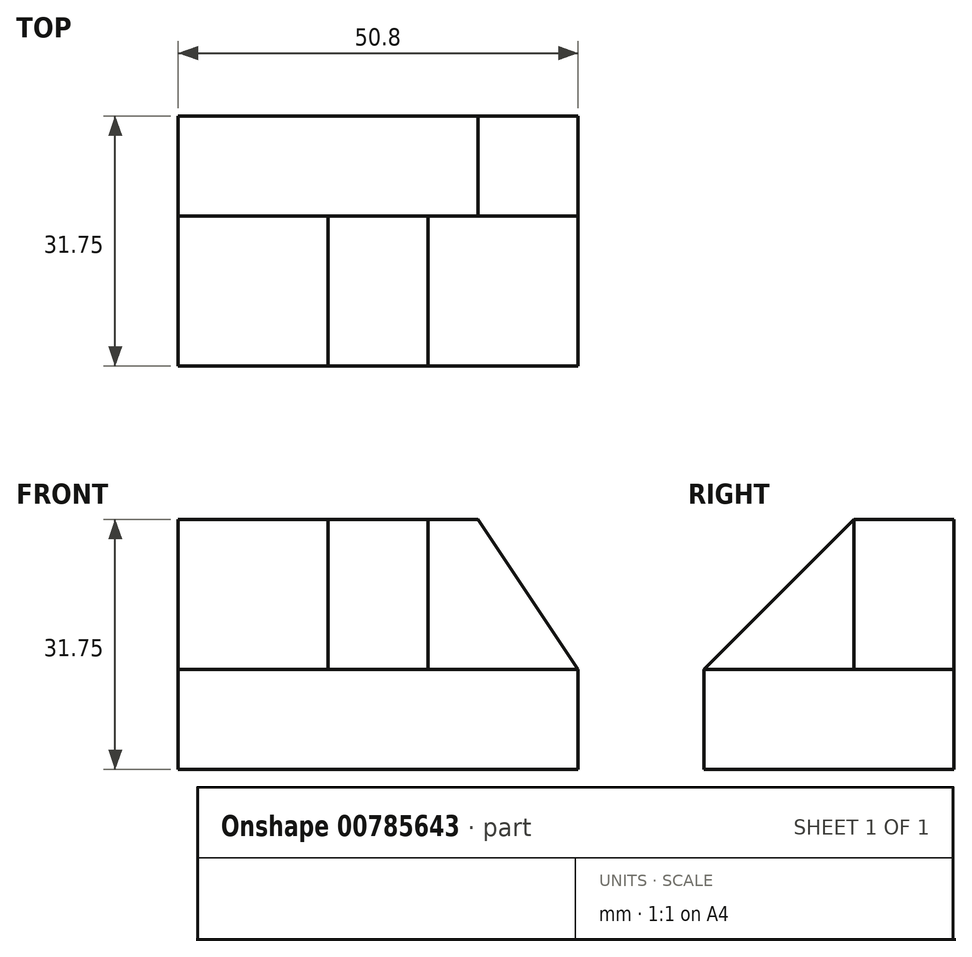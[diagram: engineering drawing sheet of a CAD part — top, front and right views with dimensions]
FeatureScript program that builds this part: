
annotation { "Feature Type Name" : "Feature", "Feature Type Description" : "" }
export const myFeature = defineFeature(function(context is Context, id is Id, definition is map)
    precondition{}
    {
        {
            var Q0;
            Q0=qCreatedBy(makeId("Front.planeOp"),FACE);
            var sketch = newSketch(context, id + "F0", { "sketchPlane" : qUnion([Q0])});
            skLineSegment(sketch, "E0", {"start": v(0, 0) * mm, "end": v(-50.8, 0) * mm});
            skLineSegment(sketch, "E1", {"start": v(-50.8, 0) * mm, "end": v(-50.8, 31.75) * mm});
            skLineSegment(sketch, "E2", {"start": v(-50.8, 31.75) * mm, "end": v(0, 31.75) * mm});
            skLineSegment(sketch, "E3", {"start": v(0, 31.75) * mm, "end": v(0, 0) * mm});
            skSolve(sketch);
        }
        {
            var Q0;
            Q0=makeQuery(id+"F0.imprint","IMPRINT",FACE,{"disambiguationData":[TD([[makeQuery(id+"F0.imprint","IMPRINT",EDGE,{"derivedFrom":sQuery(id+"F0.wireOp",EDGE,"E0")}),-1.0]])]});
            extrude(context, id + "F1", {"entities" : qUnion([Q0]), "depth" : 31.75 * mm, "offsetDistance" : 25.4 * mm});
        }
        {
            var Q0;
            Q0=makeQuery(id+"F1.opExtrude","CAP_FACE",FACE,{"disambiguationData":[OSD([sQuery(id+"F0.wireOp",EDGE,"E0"),sQuery(id+"F0.wireOp",EDGE,"E1"),sQuery(id+"F0.wireOp",EDGE,"E2"),sQuery(id+"F0.wireOp",EDGE,"E3")])],"isStart":false});
            var sketch = newSketch(context, id + "F2", { "sketchPlane" : qUnion([Q0])});
            skLineSegment(sketch, "E4", {"start": v(-50.8, 0) * mm, "end": v(-50.8, 12.7) * mm});
            skLineSegment(sketch, "E5", {"start": v(-50.8, 12.7) * mm, "end": v(0, 12.7) * mm});
            skLineSegment(sketch, "E6", {"start": v(0, 12.7) * mm, "end": v(0, 0) * mm});
            skLineSegment(sketch, "E7", {"start": v(0, 0) * mm, "end": v(-50.8, 0) * mm});
            skLineSegment(sketch, "E8", {"start": v(0, 12.7) * mm, "end": v(0, 31.75) * mm});
            skLineSegment(sketch, "E9", {"start": v(0, 31.75) * mm, "end": v(-19.05, 31.75) * mm});
            skLineSegment(sketch, "E10", {"start": v(-19.05, 31.75) * mm, "end": v(-19.05, 12.7) * mm});
            skLineSegment(sketch, "E11", {"start": v(-19.05, 12.7) * mm, "end": v(0, 12.7) * mm});
            skSolve(sketch);
        }
        {
            var Q0;
            Q0=makeQuery(id+"F2.imprint","IMPRINT",FACE,{"disambiguationData":[TD([[makeQuery(id+"F2.imprint","IMPRINT",EDGE,{"derivedFrom":sQuery(id+"F2.wireOp",EDGE,"E8")}),-1.0]])]});
            extrude(context, id + "F3", {"entities" : qUnion([Q0]), "operationType" : NewBodyOperationType.REMOVE, "oppositeDirection" : true, "depth" : 19.05 * mm, "offsetDistance" : 25.4 * mm});
        }
        {
            var Q0;
            Q0=makeQuery(id+"F3.boolean.opBoolean","COPY",FACE,{"derivedFrom":makeQuery(id+"F3.opExtrude","SWEPT_FACE",FACE,{"disambiguationData":[OSD([sQuery(id+"F2.wireOp",EDGE,"E10")])]})});
            var sketch = newSketch(context, id + "F4", { "sketchPlane" : qUnion([Q0])});
            skLineSegment(sketch, "E12", {"start": v(-12.7, 31.75) * mm, "end": v(-31.75, 12.7) * mm});
            skLineSegment(sketch, "E13", {"start": v(-31.75, 12.7) * mm, "end": v(-12.7, 12.7) * mm});
            skLineSegment(sketch, "E14", {"start": v(-12.7, 12.7) * mm, "end": v(-12.7, 31.75) * mm});
            skSolve(sketch);
        }
        {
            var Q0;
            Q0=makeQuery(id+"F4.imprint","IMPRINT",FACE,{"disambiguationData":[TD([[makeQuery(id+"F4.imprint","IMPRINT",EDGE,{"derivedFrom":sQuery(id+"F4.wireOp",EDGE,"E12")}),-1.0]])]});
            extrude(context, id + "F5", {"entities" : qUnion([Q0]), "operationType" : NewBodyOperationType.REMOVE, "oppositeDirection" : true, "depth" : 12.7 * mm, "offsetDistance" : 25.4 * mm});
        }
        {
            var Q0;
            Q0=makeQuery(id+"F1.opExtrude","CAP_FACE",FACE,{"disambiguationData":[OSD([sQuery(id+"F0.wireOp",EDGE,"E0"),sQuery(id+"F0.wireOp",EDGE,"E1"),sQuery(id+"F0.wireOp",EDGE,"E2"),sQuery(id+"F0.wireOp",EDGE,"E3")])],"isStart":false});
            var sketch = newSketch(context, id + "F6", { "sketchPlane" : qUnion([Q0])});
            skLineSegment(sketch, "E15", {"start": v(-31.75, 12.7) * mm, "end": v(-50.8, 12.7) * mm});
            skLineSegment(sketch, "E16", {"start": v(-50.8, 12.7) * mm, "end": v(-50.8, 31.75) * mm});
            skLineSegment(sketch, "E17", {"start": v(-50.8, 31.75) * mm, "end": v(-31.75, 31.75) * mm});
            skLineSegment(sketch, "E18", {"start": v(-31.75, 31.75) * mm, "end": v(-31.75, 12.7) * mm});
            skSolve(sketch);
        }
        {
            var Q0;
            Q0=makeQuery(id+"F6.imprint","IMPRINT",FACE,{"disambiguationData":[TD([[makeQuery(id+"F6.imprint","IMPRINT",EDGE,{"derivedFrom":sQuery(id+"F6.wireOp",EDGE,"E15")}),-1.0]])]});
            extrude(context, id + "F7", {"entities" : qUnion([Q0]), "operationType" : NewBodyOperationType.REMOVE, "oppositeDirection" : true, "depth" : 19.05 * mm, "offsetDistance" : 25.4 * mm});
        }
        {
            var Q0;
            Q0=makeQuery(id+"F3.boolean.opBoolean","COPY",FACE,{"derivedFrom":makeQuery(id+"F3.opExtrude","CAP_FACE",FACE,{"disambiguationData":[OSD([sQuery(id+"F2.wireOp",EDGE,"E8"),sQuery(id+"F2.wireOp",EDGE,"E9"),sQuery(id+"F2.wireOp",EDGE,"E10"),sQuery(id+"F2.wireOp",EDGE,"E11")])],"isStart":false})});
            var sketch = newSketch(context, id + "F8", { "sketchPlane" : qUnion([Q0])});
            skLineSegment(sketch, "E19", {"start": v(-19.05, 12.7) * mm, "end": v(-19.05, 31.75) * mm});
            skLineSegment(sketch, "E20", {"start": v(-19.05, 31.75) * mm, "end": v(-12.7, 31.75) * mm});
            skLineSegment(sketch, "E21", {"start": v(-19.05, 12.7) * mm, "end": v(0, 12.7) * mm});
            skLineSegment(sketch, "E22", {"start": v(0, 12.7) * mm, "end": v(-12.7, 31.75) * mm});
            skSolve(sketch);
        }
        {
            var Q0;
            {var subQ0=sQuery(id+"F8.wireOp",EDGE,"E22");Q0=makeQuery(id+"F8.imprint","IMPRINT",FACE,{"disambiguationData":[TD([[makeQuery(id+"F8.imprint","IMPRINT",EDGE,{"derivedFrom":subQ0}),-1.0]])]});}
            extrude(context, id + "F9", {"entities" : qUnion([Q0]), "operationType" : NewBodyOperationType.REMOVE, "oppositeDirection" : true, "depth" : 12.7 * mm, "offsetDistance" : 25.4 * mm});
        }
    });
